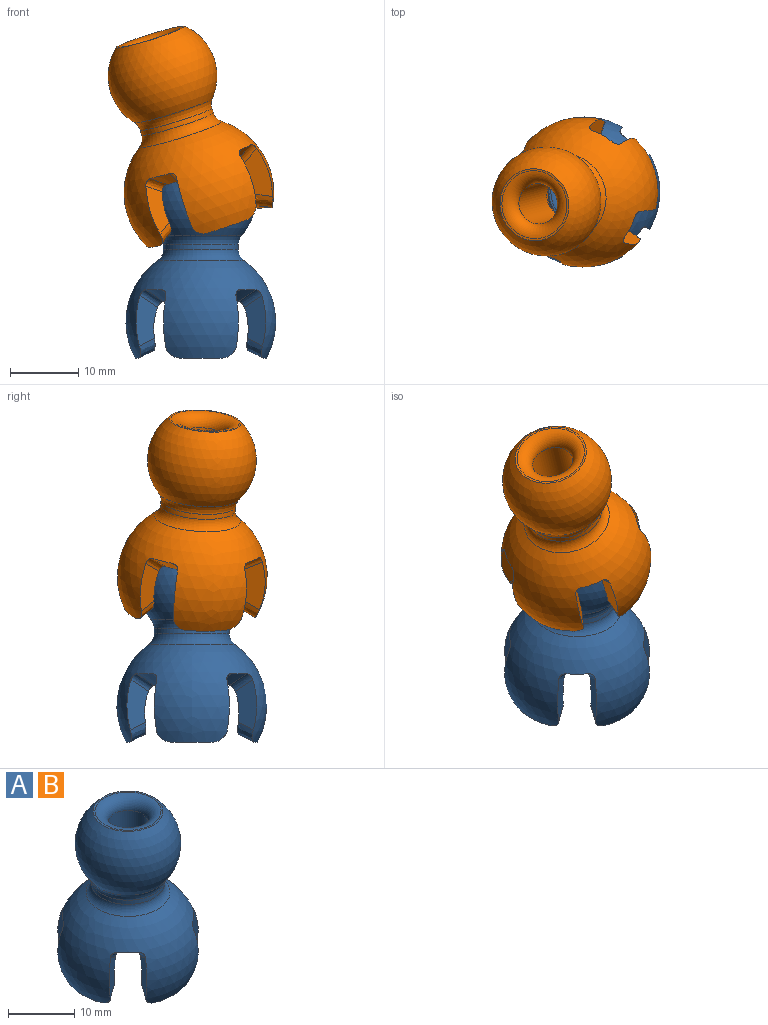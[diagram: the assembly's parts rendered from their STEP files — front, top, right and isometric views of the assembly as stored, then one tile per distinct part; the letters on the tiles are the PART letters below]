
ASSEMBLY  parts=2 mates=1
PART A: 42 faces, bbox 26.3x27.5x30.5 mm
  f0: cone r=6.93mm half-angle=60deg, axis (0,0,1), area 8.6mm2, adj f4,f9,f28,f34
  f1: cone r=6.93mm half-angle=60deg, axis (0,0,1), area 8.6mm2, adj f4,f9,f21,f27
  f2: cone r=6.93mm half-angle=60deg, axis (0,0,1), area 8.6mm2, adj f4,f9,f14,f20
  f3: cone r=6.93mm half-angle=60deg, axis (0,0,1), area 8.6mm2, adj f4,f9,f13,f35
  f4: sphere r=11mm, area 744.9mm2, adj f0,f1,f2,f3,f10,f11,f12,f13
  f5: cylinder r=5.5mm len=11mm, axis (0,0,-1), area 26.5mm2, adj f39,f40
  f6: sphere r=8mm, area 567.6mm2, adj f7,f40
  f7: plane 10.58x10.58mm, normal (0,0,1), area 9.4mm2, adj f6,f41
  f8: cylinder r=3mm len=13.78mm, axis (0,0,-1), area 259.8mm2, adj f38,f41
  f9: sphere r=8mm, area 368.4mm2, adj f0,f1,f2,f3,f10,f11,f12,f13
  f10: cone r=7.31mm half-angle=66deg, axis (0,0,-1), area 13.2mm2, adj f4,f9,f15,f16
  f11: plane 7.36x3.15mm, normal (-0.5,0.87,0), area 18.6mm2, adj f4,f9,f14,f16
  f12: plane 7.36x3.15mm, normal (-0.5,-0.87,0), area 18.6mm2, adj f4,f9,f13,f15
  f13: bspline ~8x5.58mm, area 5.2mm2, adj f3,f4,f9,f12
  f14: bspline ~8.32x5.8mm, area 5.2mm2, adj f2,f4,f9,f11
  f15: bspline ~6x4.9mm, area 8mm2, adj f4,f9,f10,f12
  f16: bspline ~6x4.9mm, area 8mm2, adj f4,f9,f10,f11
  f17: cone r=7.31mm half-angle=66deg, axis (0,0,-1), area 13.2mm2, adj f4,f9,f22,f23
  f18: plane 7.36x3.15mm, normal (-0.87,-0.5,0), area 18.6mm2, adj f4,f9,f21,f23
  f19: plane 7.36x3.15mm, normal (0.87,-0.5,0), area 18.6mm2, adj f4,f9,f20,f22
  f20: bspline ~9.2x6.38mm, area 5.2mm2, adj f2,f4,f9,f19
  f21: bspline ~8.32x5.8mm, area 5.2mm2, adj f1,f4,f9,f18
  f22: bspline ~6x4.9mm, area 8mm2, adj f4,f9,f17,f19
  f23: bspline ~6x4.9mm, area 8mm2, adj f4,f9,f17,f18
  f24: cone r=7.31mm half-angle=66deg, axis (0,0,-1), area 13.2mm2, adj f4,f9,f29,f30
  f25: plane 7.36x3.15mm, normal (0.5,-0.87,0), area 18.6mm2, adj f4,f9,f28,f30
  f26: plane 7.36x3.15mm, normal (0.5,0.87,0), area 18.6mm2, adj f4,f9,f27,f29
  f27: bspline ~9.2x6.38mm, area 5.2mm2, adj f1,f4,f9,f26
  f28: bspline ~9.52x6.6mm, area 5.2mm2, adj f0,f4,f9,f25
  f29: bspline ~6x4.9mm, area 8mm2, adj f4,f9,f24,f26
  f30: bspline ~6x4.9mm, area 8mm2, adj f4,f9,f24,f25
  f31: cone r=7.31mm half-angle=66deg, axis (0,0,-1), area 13.2mm2, adj f4,f9,f36,f37
  f32: plane 7.36x3.15mm, normal (0.87,0.5,0), area 18.6mm2, adj f4,f9,f35,f37
  f33: plane 7.36x3.15mm, normal (-0.87,0.5,0), area 18.6mm2, adj f4,f9,f34,f36
  f34: bspline ~9.2x6.38mm, area 5.2mm2, adj f0,f4,f9,f33
  f35: bspline ~9.52x6.6mm, area 5.2mm2, adj f3,f4,f9,f32
  f36: bspline ~6x4.9mm, area 8mm2, adj f4,f9,f31,f33
  f37: bspline ~6x4.9mm, area 8mm2, adj f4,f9,f31,f32
  f38: torus R=6mm, axis (0,0,-1), area 65mm2, adj f8,f9
  f39: torus R=7.5mm, axis (0,0,-1), area 69.6mm2, adj f4,f5
  f40: torus R=7.5mm, axis (0,0,1), area 51.5mm2, adj f5,f6
  f41: torus R=5mm, axis (0,0,1), area 73.6mm2, adj f7,f8
PART B: same geometry as A
PLACE A t=(-17.33,0.32,-10.18)mm fixed
PLACE B rot(axis=(0.08,-0.73,0.68),24.5deg) t=(-17.33,0.32,8.82)mm
MATE ball B.f0 <-> A.f0  axis (-0.3,-0.08,0.95) through (-17.33,0.32,8.82)mm
